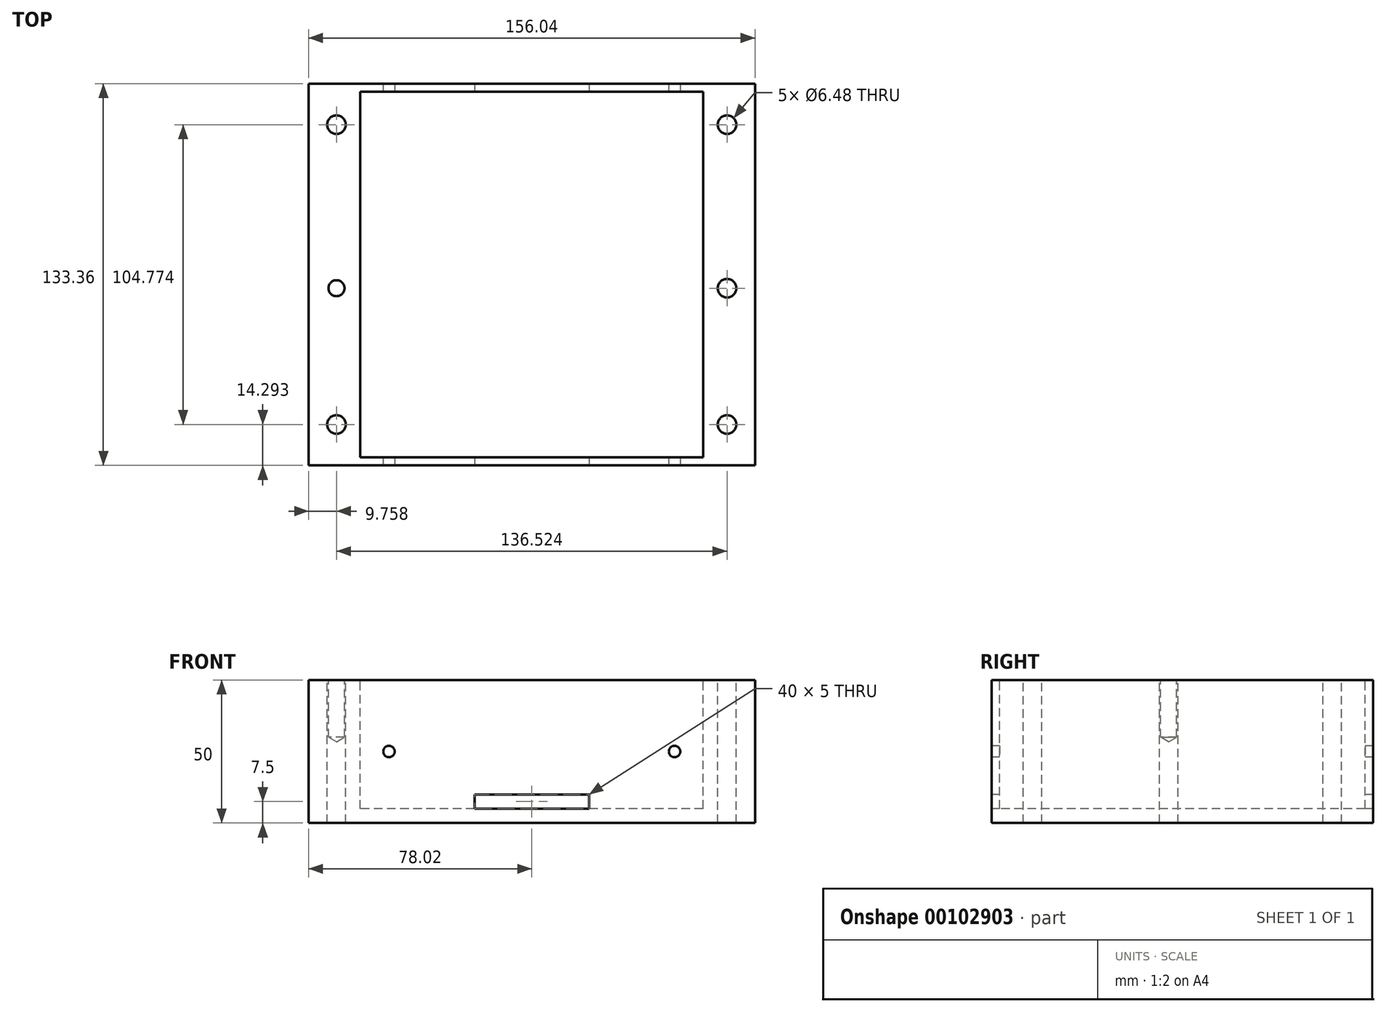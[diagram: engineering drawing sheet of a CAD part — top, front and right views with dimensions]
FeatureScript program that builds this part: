
annotation { "Feature Type Name" : "Feature", "Feature Type Description" : "" }
export const myFeature = defineFeature(function(context is Context, id is Id, definition is map)
    precondition{}
    {
        {
            var Q0;
            Q0=qCreatedBy(makeId("Top.planeOp"),FACE);
            var sketch = newSketch(context, id + "F0", { "sketchPlane" : qUnion([Q0])});
            skLineSegment(sketch, "E0", {"start": v(72.23, 1.59) * mm, "end": v(72.23, 46.04) * mm});
            skLineSegment(sketch, "E1", {"start": v(68.26, 46.04) * mm, "end": v(72.23, 46.04) * mm});
            skArc(sketch, "E2", {"start": v(68.26, 1.59) * mm, "mid": v(61.91, -4.76) * mm, "end": v(68.26, -11.11) * mm});
            skLineSegment(sketch, "E3", {"start": v(68.26, 1.59) * mm, "end": v(72.23, 1.59) * mm});
            skArc(sketch, "E4", {"start": v(68.26, -46.04) * mm, "mid": v(61.91, -52.39) * mm, "end": v(68.26, -58.74) * mm});
            skLineSegment(sketch, "E5", {"start": v(68.26, -11.11) * mm, "end": v(72.23, -11.11) * mm});
            skLineSegment(sketch, "E6", {"start": v(72.23, -46.04) * mm, "end": v(72.23, -11.11) * mm});
            skLineSegment(sketch, "E7", {"start": v(68.26, -46.04) * mm, "end": v(72.23, -46.04) * mm});
            skLineSegment(sketch, "E8", {"start": v(-72.23, -65.88) * mm, "end": v(-72.23, -58.74) * mm});
            skLineSegment(sketch, "E9", {"start": v(-68.26, -58.74) * mm, "end": v(-72.23, -58.74) * mm});
            skArc(sketch, "E10", {"start": v(-68.26, -58.74) * mm, "mid": v(-61.91, -52.39) * mm, "end": v(-68.26, -46.04) * mm});
            skLineSegment(sketch, "E11", {"start": v(72.23, -65.88) * mm, "end": v(72.23, -58.74) * mm});
            skLineSegment(sketch, "E12", {"start": v(68.26, -58.74) * mm, "end": v(72.23, -58.74) * mm});
            skLineSegment(sketch, "E13", {"start": v(72.23, -65.88) * mm, "end": v(-72.23, -65.88) * mm});
            skLineSegment(sketch, "E14", {"start": v(-68.26, -46.04) * mm, "end": v(-72.23, -46.04) * mm});
            skLineSegment(sketch, "E15", {"start": v(-68.26, 46.04) * mm, "end": v(-72.23, 46.04) * mm});
            skLineSegment(sketch, "E16", {"start": v(-72.23, 1.59) * mm, "end": v(-72.23, 46.04) * mm});
            skLineSegment(sketch, "E17", {"start": v(-68.26, 58.74) * mm, "end": v(-72.23, 58.74) * mm});
            skLineSegment(sketch, "E18", {"start": v(-72.23, 58.74) * mm, "end": v(-72.23, 65.88) * mm});
            skLineSegment(sketch, "E19", {"start": v(-72.23, 65.88) * mm, "end": v(72.23, 65.88) * mm});
            skArc(sketch, "E20", {"start": v(-68.26, 46.04) * mm, "mid": v(-61.91, 52.39) * mm, "end": v(-68.26, 58.74) * mm});
            skLineSegment(sketch, "E21", {"start": v(72.23, 58.74) * mm, "end": v(72.23, 65.88) * mm});
            skLineSegment(sketch, "E22", {"start": v(68.26, 58.74) * mm, "end": v(72.23, 58.74) * mm});
            skArc(sketch, "E23", {"start": v(68.26, 58.74) * mm, "mid": v(61.91, 52.39) * mm, "end": v(68.26, 46.04) * mm});
            skCircle(sketch, "E24", {"center": v(68.26, 52.39) * mm, "radius": 3.24 * mm});
            skCircle(sketch, "E25", {"center": v(-68.26, -52.39) * mm, "radius": 3.24 * mm});
            skCircle(sketch, "E26", {"center": v(68.26, -52.39) * mm, "radius": 3.24 * mm});
            skCircle(sketch, "E27", {"center": v(68.26, -4.76) * mm, "radius": 3.24 * mm});
            skLineSegment(sketch, "E28", {"start": v(-73.03, 66.68) * mm, "end": v(73.03, 66.68) * mm});
            skLineSegment(sketch, "E29", {"start": v(73.03, -66.68) * mm, "end": v(73.03, 66.68) * mm});
            skLineSegment(sketch, "E30", {"start": v(73.03, -66.68) * mm, "end": v(-73.03, -66.68) * mm});
            skLineSegment(sketch, "E31", {"start": v(-73.03, -66.68) * mm, "end": v(-73.03, 66.68) * mm});
            skCircle(sketch, "E32", {"center": v(-68.26, 52.39) * mm, "radius": 3.24 * mm});
            skLineSegment(sketch, "E33.MirrorCS", {"start": v(-68.26, 1.59) * mm, "end": v(-72.23, 1.59) * mm});
            skArc(sketch, "E34.MirrorCS", {"start": v(-68.26, 1.59) * mm, "mid": v(-61.91, -4.76) * mm, "end": v(-68.26, -11.11) * mm});
            skCircle(sketch, "E35.MirrorC", {"center": v(-68.26, -4.76) * mm, "radius": 3.24 * mm});
            skLineSegment(sketch, "E36.MirrorCS", {"start": v(-68.26, -11.11) * mm, "end": v(-72.23, -11.11) * mm});
            skLineSegment(sketch, "E37.MirrorCS", {"start": v(-72.23, -46.04) * mm, "end": v(-72.23, -11.11) * mm});
            skLineSegment(sketch, "E38.bottom", {"start": v(73.03, 66.68) * mm, "end": v(78.03, 66.68) * mm});
            skLineSegment(sketch, "E38.top", {"start": v(73.03, -66.68) * mm, "end": v(78.03, -66.68) * mm});
            skLineSegment(sketch, "E38.left", {"start": v(73.03, 66.68) * mm, "end": v(73.03, -66.68) * mm});
            skLineSegment(sketch, "E38.right", {"start": v(78.03, 66.68) * mm, "end": v(78.03, -66.68) * mm});
            skLineSegment(sketch, "E39.MirrorCS", {"start": v(-73.03, 66.68) * mm, "end": v(-78.03, 66.68) * mm});
            skLineSegment(sketch, "E40.MirrorCS", {"start": v(-78.03, 66.68) * mm, "end": v(-78.03, -66.68) * mm});
            skLineSegment(sketch, "E41.MirrorCS", {"start": v(-73.03, -66.68) * mm, "end": v(-78.03, -66.68) * mm});
            skSolve(sketch);
        }
        {
            var Q0;
            Q0=makeQuery(id+"F0.imprint","IMPRINT",FACE,{"disambiguationData":[TD([[makeQuery(id+"F0.imprint","IMPRINT",EDGE,{"derivedFrom":sQuery(id+"F0.wireOp",EDGE,"E31")}),1.0]])]});
            var Q1;
            Q1=makeQuery(id+"F0.imprint","IMPRINT",FACE,{"disambiguationData":[TD([[makeQuery(id+"F0.imprint","IMPRINT",EDGE,{"derivedFrom":sQuery(id+"F0.wireOp",EDGE,"E32")}),-1.0]])]});
            var Q2;
            Q2=makeQuery(id+"F0.imprint","IMPRINT",FACE,{"disambiguationData":[TD([[makeQuery(id+"F0.imprint","IMPRINT",EDGE,{"derivedFrom":sQuery(id+"F0.wireOp",EDGE,"E9")}),-1.0]])]});
            var Q3;
            Q3=makeQuery(id+"F0.imprint","IMPRINT",FACE,{"disambiguationData":[TD([[makeQuery(id+"F0.imprint","IMPRINT",EDGE,{"derivedFrom":sQuery(id+"F0.wireOp",EDGE,"E9")}),1.0]])]});
            var Q4;
            Q4=makeQuery(id+"F0.imprint","IMPRINT",FACE,{"disambiguationData":[TD([[makeQuery(id+"F0.imprint","IMPRINT",EDGE,{"derivedFrom":sQuery(id+"F0.wireOp",EDGE,"E35.MirrorC")}),1.0]])]});
            var Q5;
            Q5=makeQuery(id+"F0.imprint","IMPRINT",FACE,{"disambiguationData":[TD([[makeQuery(id+"F0.imprint","IMPRINT",EDGE,{"derivedFrom":sQuery(id+"F0.wireOp",EDGE,"E25")}),-1.0]])]});
            var Q6;
            Q6=makeQuery(id+"F0.imprint","IMPRINT",FACE,{"disambiguationData":[TD([[makeQuery(id+"F0.imprint","IMPRINT",EDGE,{"derivedFrom":sQuery(id+"F0.wireOp",EDGE,"E26")}),-1.0]])]});
            var Q7;
            Q7=makeQuery(id+"F0.imprint","IMPRINT",FACE,{"disambiguationData":[TD([[makeQuery(id+"F0.imprint","IMPRINT",EDGE,{"derivedFrom":sQuery(id+"F0.wireOp",EDGE,"E27")}),-1.0]])]});
            var Q8;
            Q8=makeQuery(id+"F0.imprint","IMPRINT",FACE,{"disambiguationData":[TD([[makeQuery(id+"F0.imprint","IMPRINT",EDGE,{"derivedFrom":sQuery(id+"F0.wireOp",EDGE,"E24")}),-1.0]])]});
            var Q9;
            Q9=makeQuery(id+"F0.imprint","IMPRINT",FACE,{"disambiguationData":[TD([[makeQuery(id+"F0.imprint","IMPRINT",EDGE,{"derivedFrom":sQuery(id+"F0.wireOp",EDGE,"E38.bottom")}),-1.0]])]});
            extrude(context, id + "F1", {"entities" : qUnion([Q0, Q1, Q2, Q3, Q4, Q5, Q6, Q7, Q8, Q9]), "oppositeDirection" : true, "depth" : 50 * mm});
        }
        {
            var Q0;
            Q0=sQuery(id+"F0.wireOp",VERTEX,"E20.center");
            var Q1;
            Q1=sQuery(id+"F0.wireOp",VERTEX,"E34.MirrorCS.center");
            var Q2;
            Q2=sQuery(id+"F0.wireOp",VERTEX,"E10.center");
            var Q3;
            Q3=sQuery(id+"F0.wireOp",VERTEX,"E4.center");
            var Q4;
            Q4=sQuery(id+"F0.wireOp",VERTEX,"E2.center");
            var Q5;
            Q5=sQuery(id+"F0.wireOp",VERTEX,"E23.center");
            var Q6;
            Q6=makeQuery(id+"F1.opExtrude","SWEPT_BODY",BODY,{"disambiguationData":[OSD([sQuery(id+"F0.wireOp",EDGE,"E28"),sQuery(id+"F0.wireOp",EDGE,"E30"),sQuery(id+"F0.wireOp",EDGE,"E38.bottom"),sQuery(id+"F0.wireOp",EDGE,"E38.top"),sQuery(id+"F0.wireOp",EDGE,"E38.right"),sQuery(id+"F0.wireOp",EDGE,"E39.MirrorCS"),sQuery(id+"F0.wireOp",EDGE,"E40.MirrorCS"),sQuery(id+"F0.wireOp",EDGE,"E41.MirrorCS")])]});
            hole(context, id + "F2", {"style" : HoleStyle.SIMPLE, "endStyle" : HoleEndStyle.BLIND, "holeDiameter" : 5.6 * mm, "holeDepth" : 20 * mm, "locations" : qUnion([Q0, Q1, Q2, Q3, Q4, Q5]), "scope" : qUnion([Q6])});
        }
        {
            var Q0;
            Q0=makeQuery(id+"F0.imprint","IMPRINT",FACE,{"disambiguationData":[TD([[makeQuery(id+"F0.imprint","IMPRINT",EDGE,{"derivedFrom":sQuery(id+"F0.wireOp",EDGE,"E9")}),1.0]])]});
            var sketch = newSketch(context, id + "F3", { "sketchPlane" : qUnion([Q0])});
            skLineSegment(sketch, "E42.bottom", {"start": v(59.91, 63.88) * mm, "end": v(-59.91, 63.88) * mm});
            skLineSegment(sketch, "E42.top", {"start": v(59.91, -63.88) * mm, "end": v(-59.91, -63.88) * mm});
            skLineSegment(sketch, "E42.left", {"start": v(59.91, 63.88) * mm, "end": v(59.91, -63.88) * mm});
            skLineSegment(sketch, "E42.right", {"start": v(-59.91, 63.88) * mm, "end": v(-59.91, -63.88) * mm});
            skPoint(sketch, "E42.middle", {"position": v(0, 0) * mm});
            skSolve(sketch);
        }
        {
            var Q0;
            Q0 = qSketchRegion(id + "F3", true);
            extrude(context, id + "F4", {"entities" : qUnion([Q0]), "operationType" : NewBodyOperationType.REMOVE, "oppositeDirection" : true, "depth" : 45 * mm});
        }
        {
            var Q0;
            Q0=makeQuery(id+"F1.opExtrude","SWEPT_FACE",FACE,{"disambiguationData":[OSD([sQuery(id+"F0.wireOp",EDGE,"E30"),sQuery(id+"F0.wireOp",EDGE,"E38.top"),sQuery(id+"F0.wireOp",EDGE,"E41.MirrorCS")])]});
            var sketch = newSketch(context, id + "F5", { "sketchPlane" : qUnion([Q0])});
            skLineSegment(sketch, "E43.bottom", {"start": v(20, -40) * mm, "end": v(-20, -40) * mm});
            skLineSegment(sketch, "E43.top", {"start": v(20, -45) * mm, "end": v(-20, -45) * mm});
            skLineSegment(sketch, "E43.left", {"start": v(20, -40) * mm, "end": v(20, -45) * mm});
            skLineSegment(sketch, "E43.right", {"start": v(-20, -40) * mm, "end": v(-20, -45) * mm});
            skPoint(sketch, "E43.middle", {"position": v(0, -42.5) * mm});
            skPoint(sketch, "E44", {"position": v(-49.91, -25) * mm});
            skPoint(sketch, "E45.MirrorP", {"position": v(49.91, -25) * mm});
            skSolve(sketch);
        }
        {
            var Q0;
            Q0=makeQuery(id+"F5.imprint","IMPRINT",FACE,{"disambiguationData":[TD([[makeQuery(id+"F5.imprint","IMPRINT",EDGE,{"derivedFrom":sQuery(id+"F5.wireOp",EDGE,"E43.bottom")}),1.0]])]});
            extrude(context, id + "F6", {"entities" : qUnion([Q0]), "operationType" : NewBodyOperationType.REMOVE, "endBound" : BoundingType.THROUGH_ALL, "oppositeDirection" : true, "depth" : 25 * mm});
        }
        {
            var Q0;
            Q0=sQuery(id+"F5.wireOp",VERTEX,"E44");
            var Q1;
            Q1=sQuery(id+"F5.wireOp",VERTEX,"E45.MirrorP");
            var Q2;
            Q2=makeQuery(id+"F1.opExtrude","SWEPT_BODY",BODY,{"disambiguationData":[OSD([sQuery(id+"F0.wireOp",EDGE,"E28"),sQuery(id+"F0.wireOp",EDGE,"E30"),sQuery(id+"F0.wireOp",EDGE,"E38.bottom"),sQuery(id+"F0.wireOp",EDGE,"E38.top"),sQuery(id+"F0.wireOp",EDGE,"E38.right"),sQuery(id+"F0.wireOp",EDGE,"E39.MirrorCS"),sQuery(id+"F0.wireOp",EDGE,"E40.MirrorCS"),sQuery(id+"F0.wireOp",EDGE,"E41.MirrorCS")])]});
            hole(context, id + "F7", {"style" : HoleStyle.SIMPLE, "endStyle" : HoleEndStyle.THROUGH, "holeDiameter" : 4 * mm, "locations" : qUnion([Q0, Q1]), "scope" : qUnion([Q2]), "isTappedThrough" : true});
        }
    });
